# Revit family: puz-zrmp28_63ska12_60Hz
name_source: partatom
category: 機械設備
units: mm (PartAtom-declared; Revit-internal decimal feet)

## family parameters
OmniClass タイトル = Split System Air Conditioning Units
OmniClass 番号 = 23.75.10.24.21.27.27
パーツ タイプ = 標準
ロード時にボイドで切り取り = いいえ
丸型コネクタ寸法 = 直径を使用
作業面ベース = いいえ
共有 = いいえ
常に垂直 = はい
部屋計算ポイント = いいえ

## types (12) — shared parameters
Clearance Back = 100  [stored 0.328084 ft]
Clearance Front = 500  [stored 1.64042 ft]
Clearance Left = 100  [stored 0.328084 ft]
Clearance Right = 350  [stored 1.14829 ft]
Clearance Top = 100  [stored 0.328084 ft]
Depth = 300
Height = 630  [stored 2.06693 ft]
IfcExportAs = IfcUnitaryEquipmentType
IfcExportType = AIRCONDITIONINGUNIT
OmniClassCode = 23-33 17 13 11
URL = https://www.mitsubishielectric.co.jp
Uniclass2015Code = Pr_70_65_03_84
Uniclass2015Title = Split coil remote air cooled condensing units
Uniclass2015Version = Systems v1.9
Width = 809  [stored 2.6542 ft]
アンカーボルト位置X = 500  [stored 1.64042 ft]
アンカーボルト位置Y = 330  [stored 1.08268 ft]
サービススペース = はい
ドレン　位置X = 404.5  [stored 1.3271 ft]
ドレン　位置Y = 48.5  [stored 0.159121 ft]
ドレン　位置Z = 8.5  [stored 0.0278871 ft]
ドレン管径 = 42.00 mm
ユニット2 = はい
ユニット3 = はい
ユニット数 = 1
仕様書バージョン = Version1.0
企業コード = 108420
冷媒ガス管径 = 12.70 mm
冷媒液管径 = 6.35 mm
冷媒管位置X = 420  [stored 1.37795 ft]
冷媒管位置Y = 153.75  [stored 0.504429 ft]
冷媒管位置Z = 158.95
冷媒管径 = 60.00 mm
冷媒管径符号 = Ac
冷媒管（ガス）位置X = 420  [stored 1.37795 ft]
冷媒管（ガス）位置Y = 153.75  [stored 0.504429 ft]
冷媒管（液）位置X = 420  [stored 1.37795 ft]
冷媒管（液）位置Y = 153.75  [stored 0.504429 ft]
分類コード = 50053003126100
参照している仕様書等のバージョン = 公共建築物標準仕様書（機械設備工事編）平成31年度版
周波数 = 60 Hz
呼称 = パッケージ形空気調和機_室外機
始動方式 = インバータ始動方式
形名 = PUZ-ZRMP-1
形式 = パッケージ形 室外機
最大電流値 = 0 A
最小電線太さ_mm2 = 1.6
本体マテリアル = <カテゴリ別>
法定耐用年数 = 6
消費電力 = 1 kW
消費電力_冷房 = 1 kW
消費電力_暖房 = 1 kW
発停方法 = 付属スイッチ
積算_科目 = 1 空気調和設備
符号 = PAC
製品リリース年月 = 2022/10/11
製品出荷対象 = 国内
製造元 = 三菱電機株式会社
設置方法 = 床置形
説明 = 空冷H/P PAC インバータ室外機
負荷分類 = 1_熱源類
運転方法 = 冷暖切替
運転質量 = 0.00 kg
電動機出力_圧縮機 = 1 kW
電動機出力_送風機 = 0 kW
電圧 = 200 V
電源位置X = 400  [stored 1.31234 ft]
電源位置Y = 61  [stored 0.200131 ft]
電源位置Z = 497.7  [stored 1.63287 ft]
zero-valued in all types: APF, COP, Clearance Bottom, 据付ピッチ1

## per-type parameters (varying)
| type | 価格 | 冷房能力 | 推奨ブレーカー容量 | 暖房能力 | 極数 | 構成品番 | 相 | 製品質量 | 質量 | 音響パワーレベル(dB) | 音響パワーレベル（冷）(dB) |
| PUZ-ZRMP28SKA12 | 480000 $ | 3 kW | 20 A | 3 kW | 1 | PUZ-ZRMP28SKA | 1 | 37.00 kg | 44.40 kg | 66 | 64 |
| PUZ-ZRMP28KA12 | 480000 $ | 3 kW | 15 A | 3 kW | 3 | PUZ-ZRMP28KA | 3 | 36.00 kg | 43.20 kg | 66 | 64 |
| PUZ-ZRMP40SKA12 | 521000 $ | 4 kW | 20 A | 4 kW | 1 | PUZ-ZRMP40SKA | 1 | 43.00 kg | 51.60 kg | 66 | 64 |
| PUZ-ZRMP40KA12 | 521000 $ | 4 kW | 15 A | 4 kW | 3 | PUZ-ZRMP40KA | 3 | 41.00 kg | 49.20 kg | 66 | 64 |
| PUZ-ZRMP45SKA12 | 573000 $ | 4 kW | 20 A | 5 kW | 1 | PUZ-ZRMP45SKA | 1 | 43.00 kg | 51.60 kg | 66 | 64 |
| PUZ-ZRMP45KA12 | 573000 $ | 4 kW | 15 A | 5 kW | 3 | PUZ-ZRMP45KA | 3 | 41.00 kg | 49.20 kg | 66 | 64 |
| PUZ-ZRMP50SKA12 | 621000 $ | 5 kW | 20 A | 5 kW | 1 | PUZ-ZRMP50SKA | 1 | 43.00 kg | 51.60 kg | 67 | 65 |
| PUZ-ZRMP50KA12 | 621000 $ | 5 kW | 15 A | 5 kW | 3 | PUZ-ZRMP50KA | 3 | 41.00 kg | 49.20 kg | 67 | 65 |
| PUZ-ZRMP56SKA12 | 662000 $ | 5 kW | 20 A | 6 kW | 1 | PUZ-ZRMP56SKA | 1 | 43.00 kg | 51.60 kg | 67 | 65 |
| PUZ-ZRMP56KA12 | 662000 $ | 5 kW | 15 A | 6 kW | 3 | PUZ-ZRMP56KA | 3 | 41.00 kg | 49.20 kg | 67 | 65 |
| PUZ-ZRMP63SKA12 | 716000 $ | 6 kW | 30 A | 6 kW | 1 | PUZ-ZRMP63SKA | 1 | 43.00 kg | 51.60 kg | 67 | 65 |
| PUZ-ZRMP63KA12 | 716000 $ | 6 kW | 15 A | 6 kW | 3 | PUZ-ZRMP63KA | 3 | 42.00 kg | 50.40 kg | 67 | 65 |

note: [stored X ft] marks values corroborated as IEEE doubles in the binary element streams (Revit-internal decimal feet)
